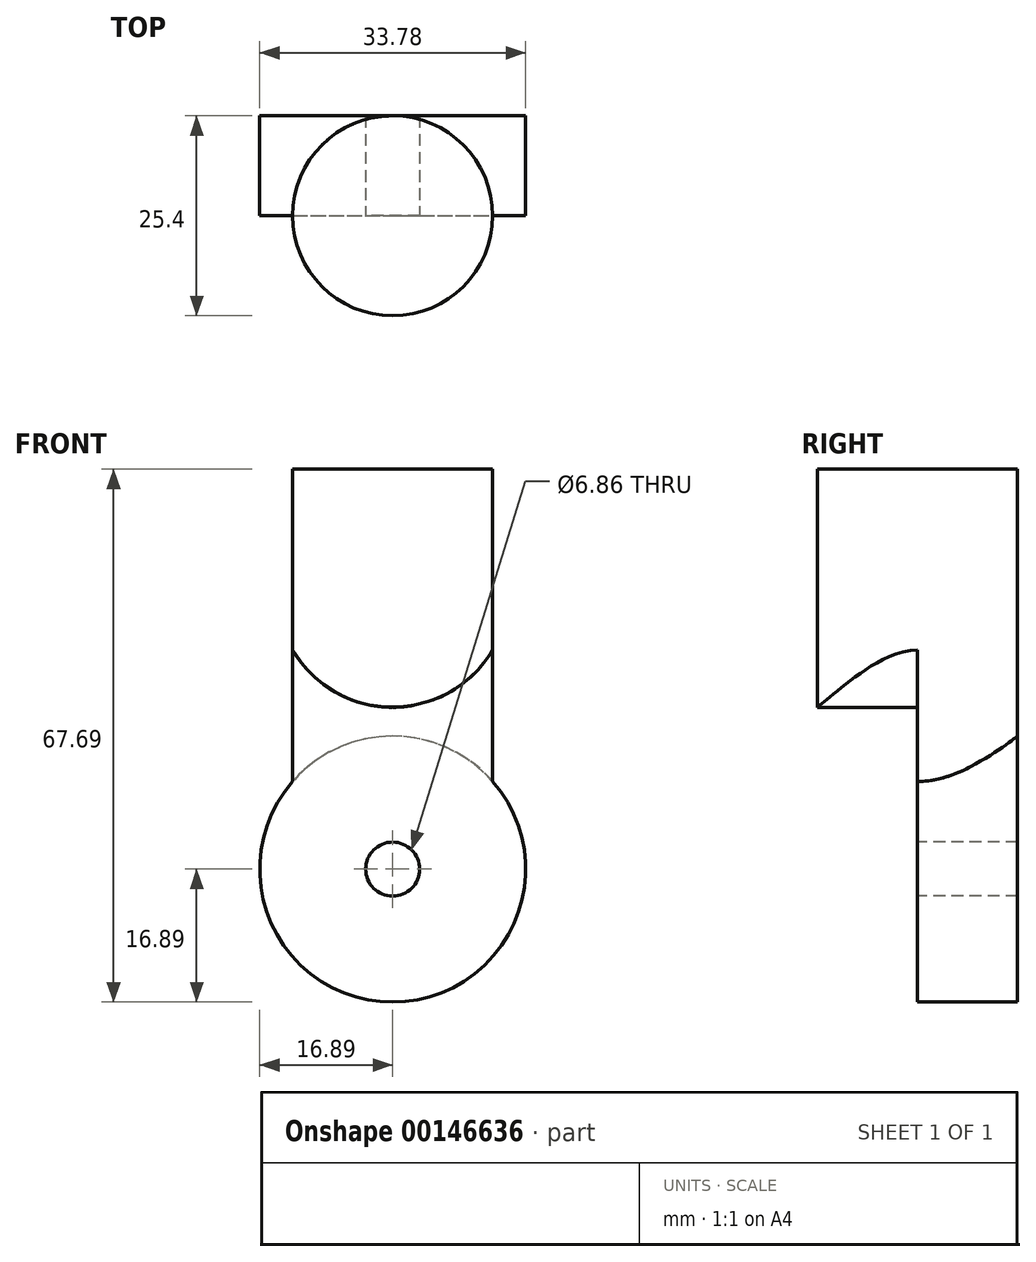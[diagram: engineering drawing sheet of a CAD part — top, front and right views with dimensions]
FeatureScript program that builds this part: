
annotation { "Feature Type Name" : "Feature", "Feature Type Description" : "" }
export const myFeature = defineFeature(function(context is Context, id is Id, definition is map)
    precondition{}
    {
        {
            var Q0;
            Q0=qCreatedBy(makeId("Front.planeOp"),FACE);
            var sketch = newSketch(context, id + "F0", { "sketchPlane" : qUnion([Q0])});
            skCircle(sketch, "E0", {"center": v(0, 0) * mm, "radius": 16.9 * mm});
            skSolve(sketch);
        }
        {
            var Q0;
            Q0 = qSketchRegion(id + "F0", true);
            extrude(context, id + "F1", {"entities" : qUnion([Q0]), "endBound" : BoundingType.SYMMETRIC, "depth" : 25.4 * mm});
        }
        {
            var Q0;
            Q0=qCreatedBy(makeId("Top.planeOp"),FACE);
            var sketch = newSketch(context, id + "F2", { "sketchPlane" : qUnion([Q0])});
            skCircle(sketch, "E1", {"center": v(0, 0) * mm, "radius": 12.7 * mm});
            skLineSegment(sketch, "E2", {"start": v(20.17, 0) * mm, "end": v(-31.4, 0) * mm, "construction": true});
            skSolve(sketch);
        }
        {
            var Q0;
            Q0 = qSketchRegion(id + "F2", true);
            extrude(context, id + "F3", {"entities" : qUnion([Q0]), "operationType" : NewBodyOperationType.ADD, "depth" : 50.8 * mm});
        }
        {
            var Q0;
            Q0=qCreatedBy(makeId("Front.planeOp"),FACE);
            cPlane(context, id + "F4", {"entities" : qUnion([Q0]), "cplaneType" : CPlaneType.OFFSET, "offset" : 12.7 * mm, "width" : 152.4 * mm, "height" : 152.4 * mm});
        }
        {
            var Q0;
            Q0=qCreatedBy(id+"F4.planeOp",FACE);
            var sketch = newSketch(context, id + "F5", { "sketchPlane" : qUnion([Q0])});
            skCircle(sketch, "E3", {"center": v(0, 0) * mm, "radius": 16.9 * mm});
            skSolve(sketch);
        }
        {
            var Q0;
            Q0 = qSketchRegion(id + "F5", true);
            var Q1;
            Q1=makeQuery(id+"F1.opExtrude","CAP_FACE",FACE,{"disambiguationData":[OSD([sQuery(id+"F0.wireOp",EDGE,"E0")])],"isStart":false});
            extrude(context, id + "F6", {"entities" : qUnion([Q0]), "operationType" : NewBodyOperationType.REMOVE, "oppositeDirection" : true, "endBoundEntityFace" : qUnion([Q1]), "depth" : 12.7 * mm});
        }
        {
            var Q0;
            Q0=makeQuery(id+"F6.boolean.opBoolean","COPY",FACE,{"derivedFrom":makeQuery(id+"F6.opExtrude","CAP_FACE",FACE,{"disambiguationData":[OSD([sQuery(id+"F5.wireOp",EDGE,"E3")])],"isStart":false})});
            var sketch = newSketch(context, id + "F7", { "sketchPlane" : qUnion([Q0])});
            skCircle(sketch, "E4", {"center": v(0, 0) * mm, "radius": 3.43 * mm});
            skSolve(sketch);
        }
        {
            var Q0;
            Q0 = qSketchRegion(id + "F7", true);
            extrude(context, id + "F8", {"entities" : qUnion([Q0]), "operationType" : NewBodyOperationType.REMOVE, "endBound" : BoundingType.THROUGH_ALL, "oppositeDirection" : true, "depth" : 25.4 * mm});
        }
        {
            var Q0;
            Q0=qCreatedBy(id+"F4.planeOp",FACE);
            var sketch = newSketch(context, id + "F9", { "sketchPlane" : qUnion([Q0])});
            skArc(sketch, "E5", {"start": v(-13.43, 29.26) * mm, "mid": v(0, 20.56) * mm, "end": v(13.43, 29.26) * mm});
            skLineSegment(sketch, "E6.bottom", {"start": v(13.43, 29.26) * mm, "end": v(13.45, 29.26) * mm});
            skLineSegment(sketch, "E6.top", {"start": v(-13.43, 6.1) * mm, "end": v(13.45, 6.1) * mm});
            skLineSegment(sketch, "E6.left", {"start": v(-13.43, 29.26) * mm, "end": v(-13.43, 6.1) * mm});
            skLineSegment(sketch, "E6.right", {"start": v(13.45, 29.26) * mm, "end": v(13.45, 6.1) * mm});
            skPoint(sketch, "E7.orphan", {"position": v(-14.72, 35.29) * mm});
            skSolve(sketch);
        }
        {
            var Q0;
            Q0 = qSketchRegion(id + "F9", true);
            var Q1;
            Q1=makeQuery(id+"F6.boolean.opBoolean","COPY",FACE,{"derivedFrom":makeQuery(id+"F6.opExtrude","CAP_FACE",FACE,{"disambiguationData":[OSD([sQuery(id+"F5.wireOp",EDGE,"E3")])],"isStart":false})});
            extrude(context, id + "F10", {"entities" : qUnion([Q0]), "operationType" : NewBodyOperationType.REMOVE, "endBound" : BoundingType.UP_TO_SURFACE, "oppositeDirection" : true, "endBoundEntityFace" : qUnion([Q1]), "depth" : 25.4 * mm});
        }
    });
